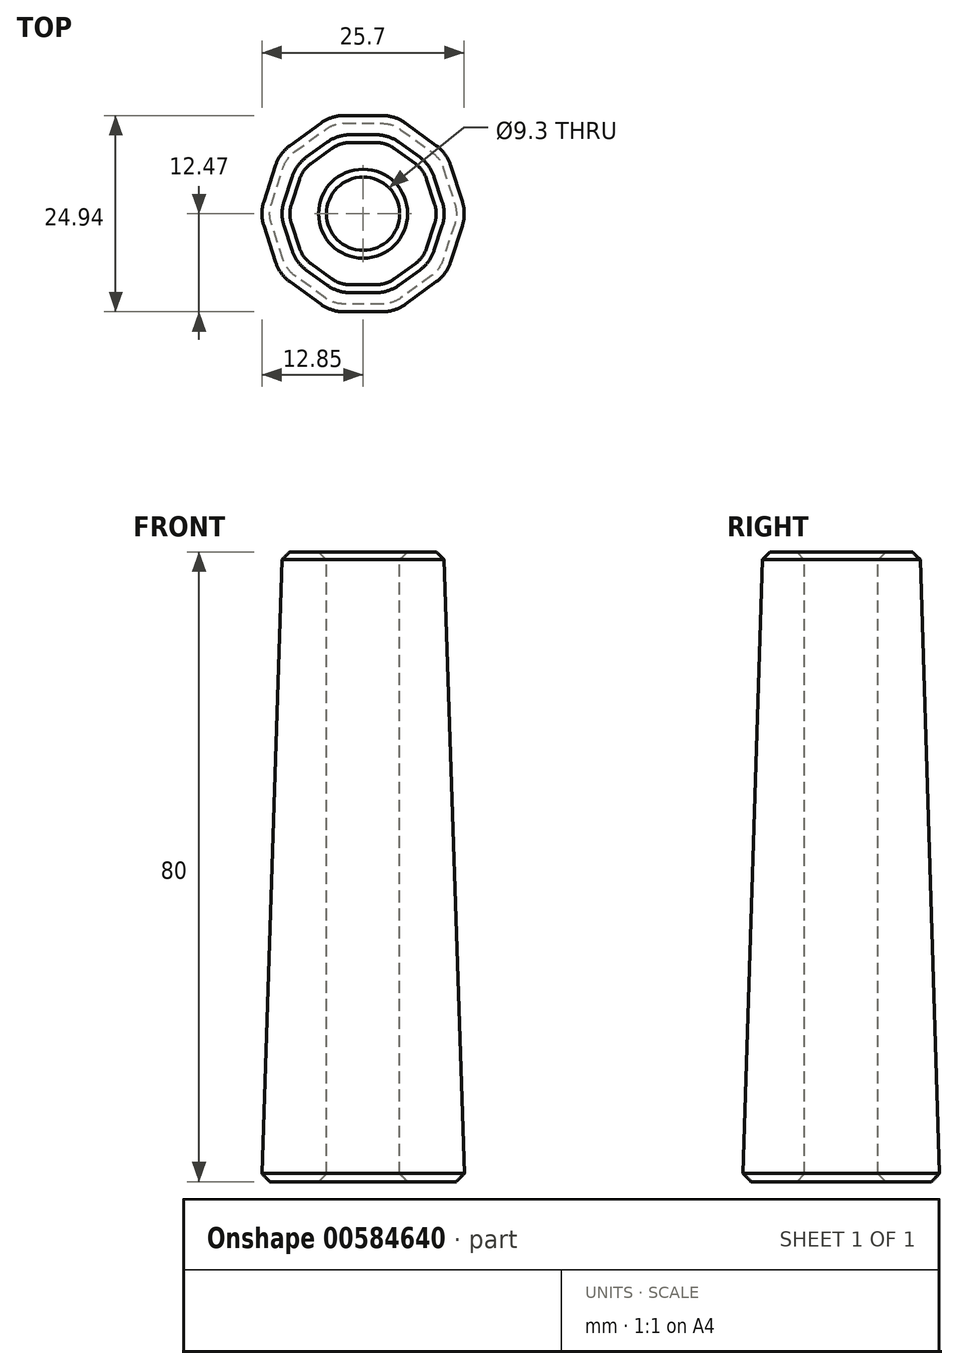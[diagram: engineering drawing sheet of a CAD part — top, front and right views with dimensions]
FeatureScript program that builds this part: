
annotation { "Feature Type Name" : "Feature", "Feature Type Description" : "" }
export const myFeature = defineFeature(function(context is Context, id is Id, definition is map)
    precondition{}
    {
        {
            var Q0;
            Q0=qCreatedBy(makeId("Top.planeOp"),FACE);
            var sketch = newSketch(context, id + "F0", { "sketchPlane" : qUnion([Q0])});
            skCircle(sketch, "E0.cCircle", {"center": v(0, 0) * mm, "radius": 12.5 * mm, "construction": true});
            skLineSegment(sketch, "E0.0", {"start": v(10.63, -7.73) * mm, "end": v(4.06, -12.5) * mm});
            skLineSegment(sketch, "E0.1", {"start": v(4.06, -12.5) * mm, "end": v(-4.06, -12.5) * mm});
            skLineSegment(sketch, "E0.2", {"start": v(-4.06, -12.5) * mm, "end": v(-10.63, -7.73) * mm});
            skLineSegment(sketch, "E0.3", {"start": v(-10.63, -7.73) * mm, "end": v(-13.14, 0) * mm});
            skLineSegment(sketch, "E0.4", {"start": v(-13.14, 0) * mm, "end": v(-10.63, 7.73) * mm});
            skLineSegment(sketch, "E0.5", {"start": v(-10.63, 7.73) * mm, "end": v(-4.06, 12.5) * mm});
            skLineSegment(sketch, "E0.6", {"start": v(-4.06, 12.5) * mm, "end": v(4.06, 12.5) * mm});
            skLineSegment(sketch, "E0.7", {"start": v(4.06, 12.5) * mm, "end": v(10.63, 7.73) * mm});
            skLineSegment(sketch, "E0.8", {"start": v(10.63, 7.73) * mm, "end": v(13.14, 0) * mm});
            skLineSegment(sketch, "E0.9", {"start": v(13.14, 0) * mm, "end": v(10.63, -7.73) * mm});
            skPoint(sketch, "E0.0.midPoint", {"position": v(7.35, -10.11) * mm});
            skSolve(sketch);
        }
        {
            var Q0;
            Q0=qCreatedBy(makeId("Top.planeOp"),FACE);
            cPlane(context, id + "F1", {"entities" : qUnion([Q0]), "cplaneType" : CPlaneType.OFFSET, "offset" : 80 * mm, "width" : 150 * mm, "height" : 150 * mm});
        }
        {
            var Q0;
            Q0=qCreatedBy(id+"F1.planeOp",FACE);
            var sketch = newSketch(context, id + "F2", { "sketchPlane" : qUnion([Q0])});
            skCircle(sketch, "E1.cCircle", {"center": v(0, 0) * mm, "radius": 10 * mm, "construction": true});
            skLineSegment(sketch, "E1.0", {"start": v(10.51, 0) * mm, "end": v(8.5, -6.18) * mm});
            skLineSegment(sketch, "E1.1", {"start": v(8.5, -6.18) * mm, "end": v(3.25, -10) * mm});
            skLineSegment(sketch, "E1.2", {"start": v(3.25, -10) * mm, "end": v(-3.25, -10) * mm});
            skLineSegment(sketch, "E1.3", {"start": v(-3.25, -10) * mm, "end": v(-8.5, -6.18) * mm});
            skLineSegment(sketch, "E1.4", {"start": v(-8.5, -6.18) * mm, "end": v(-10.51, 0) * mm});
            skLineSegment(sketch, "E1.5", {"start": v(-10.51, 0) * mm, "end": v(-8.5, 6.18) * mm});
            skLineSegment(sketch, "E1.6", {"start": v(-8.5, 6.18) * mm, "end": v(-3.25, 10) * mm});
            skLineSegment(sketch, "E1.7", {"start": v(-3.25, 10) * mm, "end": v(3.25, 10) * mm});
            skLineSegment(sketch, "E1.8", {"start": v(3.25, 10) * mm, "end": v(8.5, 6.18) * mm});
            skLineSegment(sketch, "E1.9", {"start": v(8.5, 6.18) * mm, "end": v(10.51, 0) * mm});
            skPoint(sketch, "E1.0.midPoint", {"position": v(9.51, -3.1) * mm});
            skSolve(sketch);
        }
        {
            var Q0;
            Q0=makeQuery(id+"F2.imprint","IMPRINT",FACE,{"disambiguationData":[TD([[makeQuery(id+"F2.imprint","IMPRINT",EDGE,{"derivedFrom":sQuery(id+"F2.wireOp",EDGE,"E1.0")}),-1.0]])]});
            var Q1;
            Q1=makeQuery(id+"F0.imprint","IMPRINT",FACE,{"disambiguationData":[TD([[makeQuery(id+"F0.imprint","IMPRINT",EDGE,{"derivedFrom":sQuery(id+"F0.wireOp",EDGE,"E0.0")}),-1.0]])]});
            loft(context, id + "F3", {"sheetProfilesArray" : [{ "sheetProfileEntities" : qUnion([Q0]) }, { "sheetProfileEntities" : qUnion([Q1]) }]});
        }
        {
            var Q0;
            Q0=makeQuery(id+"F3.opLoft","SWEPT_EDGE",EDGE,{"disambiguationData":[OSD([sQuery(id+"F0.wireOp",EDGE,"E0.1"),sQuery(id+"F0.wireOp",EDGE,"E0.2"),sQuery(id+"F2.wireOp",EDGE,"E1.2"),sQuery(id+"F2.wireOp",EDGE,"E1.3")])]});
            var Q1;
            Q1=makeQuery(id+"F3.opLoft","SWEPT_EDGE",EDGE,{"disambiguationData":[OSD([sQuery(id+"F0.wireOp",EDGE,"E0.0"),sQuery(id+"F0.wireOp",EDGE,"E0.1"),sQuery(id+"F2.wireOp",EDGE,"E1.1"),sQuery(id+"F2.wireOp",EDGE,"E1.2")])]});
            var Q2;
            Q2=makeQuery(id+"F3.opLoft","SWEPT_EDGE",EDGE,{"disambiguationData":[OSD([sQuery(id+"F0.wireOp",EDGE,"E0.0"),sQuery(id+"F0.wireOp",EDGE,"E0.9"),sQuery(id+"F2.wireOp",EDGE,"E1.0"),sQuery(id+"F2.wireOp",EDGE,"E1.1")])]});
            var Q3;
            Q3=makeQuery(id+"F3.opLoft","SWEPT_EDGE",EDGE,{"disambiguationData":[OSD([sQuery(id+"F0.wireOp",EDGE,"E0.2"),sQuery(id+"F0.wireOp",EDGE,"E0.3"),sQuery(id+"F2.wireOp",EDGE,"E1.3"),sQuery(id+"F2.wireOp",EDGE,"E1.4")])]});
            var Q4;
            Q4=makeQuery(id+"F3.opLoft","SWEPT_EDGE",EDGE,{"disambiguationData":[OSD([sQuery(id+"F0.wireOp",EDGE,"E0.3"),sQuery(id+"F0.wireOp",EDGE,"E0.4"),sQuery(id+"F2.wireOp",EDGE,"E1.4"),sQuery(id+"F2.wireOp",EDGE,"E1.5")])]});
            var Q5;
            Q5=makeQuery(id+"F3.opLoft","SWEPT_EDGE",EDGE,{"disambiguationData":[OSD([sQuery(id+"F0.wireOp",EDGE,"E0.4"),sQuery(id+"F0.wireOp",EDGE,"E0.5"),sQuery(id+"F2.wireOp",EDGE,"E1.5"),sQuery(id+"F2.wireOp",EDGE,"E1.6")])]});
            var Q6;
            Q6=makeQuery(id+"F3.opLoft","SWEPT_EDGE",EDGE,{"disambiguationData":[OSD([sQuery(id+"F0.wireOp",EDGE,"E0.5"),sQuery(id+"F0.wireOp",EDGE,"E0.6"),sQuery(id+"F2.wireOp",EDGE,"E1.6"),sQuery(id+"F2.wireOp",EDGE,"E1.7")])]});
            var Q7;
            Q7=makeQuery(id+"F3.opLoft","SWEPT_EDGE",EDGE,{"disambiguationData":[OSD([sQuery(id+"F0.wireOp",EDGE,"E0.6"),sQuery(id+"F0.wireOp",EDGE,"E0.7"),sQuery(id+"F2.wireOp",EDGE,"E1.7"),sQuery(id+"F2.wireOp",EDGE,"E1.8")])]});
            var Q8;
            Q8=makeQuery(id+"F3.opLoft","SWEPT_EDGE",EDGE,{"disambiguationData":[OSD([sQuery(id+"F0.wireOp",EDGE,"E0.7"),sQuery(id+"F0.wireOp",EDGE,"E0.8"),sQuery(id+"F2.wireOp",EDGE,"E1.8"),sQuery(id+"F2.wireOp",EDGE,"E1.9")])]});
            var Q9;
            Q9=makeQuery(id+"F3.opLoft","SWEPT_EDGE",EDGE,{"disambiguationData":[OSD([sQuery(id+"F0.wireOp",EDGE,"E0.8"),sQuery(id+"F0.wireOp",EDGE,"E0.9"),sQuery(id+"F2.wireOp",EDGE,"E1.0"),sQuery(id+"F2.wireOp",EDGE,"E1.9")])]});
            fillet(context, id + "F4", {"entities" : qUnion([Q0, Q1, Q2, Q3, Q4, Q5, Q6, Q7, Q8, Q9]), "radius" : 5 * mm, "tangentPropagation" : true, "allowEdgeOverflow" : false});
        }
        {
            var Q0;
            Q0=qCreatedBy(id+"F1.planeOp",FACE);
            var sketch = newSketch(context, id + "F5", { "sketchPlane" : qUnion([Q0])});
            skCircle(sketch, "E2", {"center": v(0, 0) * mm, "radius": 4.65 * mm});
            skSolve(sketch);
        }
        {
            var Q0;
            Q0=makeQuery(id+"F5.imprint","IMPRINT",FACE,{"disambiguationData":[TD([[makeQuery(id+"F5.imprint","IMPRINT",EDGE,{"derivedFrom":sQuery(id+"F5.wireOp",EDGE,"E2")}),1.0]])]});
            extrude(context, id + "F6", {"entities" : qUnion([Q0]), "operationType" : NewBodyOperationType.REMOVE, "oppositeDirection" : true, "depth" : 104.3 * mm, "offsetDistance" : 25 * mm});
        }
        {
            var Q0;
            Q0=makeQuery(id+"F6.boolean.opBoolean","COPY",EDGE,{"derivedFrom":makeQuery(id+"F6.opExtrude","CAP_EDGE",EDGE,{"disambiguationData":[OSD([sQuery(id+"F5.wireOp",EDGE,"E2")])],"isStart":true})});
            var Q1;
            Q1=makeQuery(id+"F3.opLoft","CAP_FACE",FACE,{"disambiguationData":[OSD([makeQuery(id+"F2.imprint","IMPRINT",FACE,{"disambiguationData":[TD([[makeQuery(id+"F2.imprint","IMPRINT",EDGE,{"derivedFrom":sQuery(id+"F2.wireOp",EDGE,"E1.0")}),-1.0]])]})])],"isStart":true});
            var Q2;
            Q2=makeQuery(id+"F3.opLoft","CAP_FACE",FACE,{"disambiguationData":[OSD([makeQuery(id+"F0.imprint","IMPRINT",FACE,{"disambiguationData":[TD([[makeQuery(id+"F0.imprint","IMPRINT",EDGE,{"derivedFrom":sQuery(id+"F0.wireOp",EDGE,"E0.0")}),-1.0]])]})])],"isStart":true});
            chamfer(context, id + "F7", {"entities" : qUnion([Q0, Q1, Q2]), "width" : 1 * mm, "tangentPropagation" : true});
        }
    });
